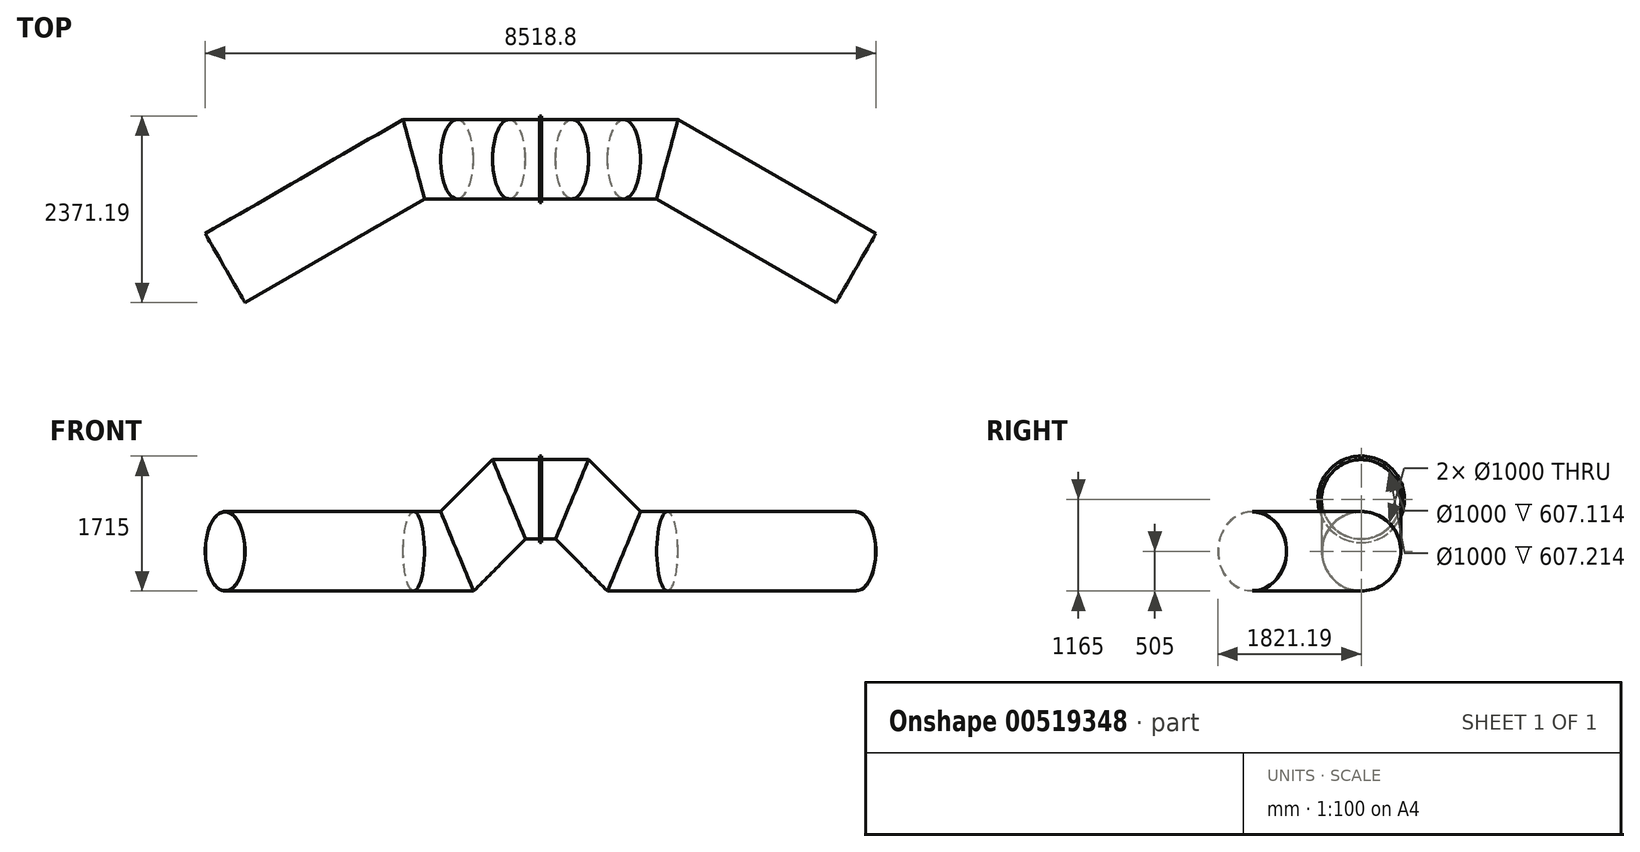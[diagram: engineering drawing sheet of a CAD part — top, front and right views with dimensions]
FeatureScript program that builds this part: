
annotation { "Feature Type Name" : "Feature", "Feature Type Description" : "" }
export const myFeature = defineFeature(function(context is Context, id is Id, definition is map)
    precondition{}
    {
        {
            var Q0;
            Q0=qCreatedBy(makeId("Top.planeOp"),FACE);
            var sketch = newSketch(context, id + "F0", { "sketchPlane" : qUnion([Q0])});
            skLineSegment(sketch, "E0", {"start": v(0, 0) * mm, "end": v(3000, 0) * mm, "construction": true});
            skSolve(sketch);
        }
        {
            var Q0;
            Q0=qCreatedBy(makeId("Top.planeOp"),FACE);
            cPlane(context, id + "F1", {"entities" : qUnion([Q0]), "cplaneType" : CPlaneType.OFFSET, "offset" : 660 * mm, "oppositeDirection" : true, "width" : 150 * mm, "height" : 150 * mm});
        }
        {
            var Q0;
            Q0=qCreatedBy(id+"F1.planeOp",FACE);
            var sketch = newSketch(context, id + "F2", { "sketchPlane" : qUnion([Q0])});
            skLineSegment(sketch, "E1", {"start": v(1610, 0) * mm, "end": v(4006.9, -1383.85) * mm});
            skLineSegment(sketch, "E2", {"start": v(4006.9, -1383.85) * mm, "end": v(3906.9, -1557.05) * mm, "construction": true});
            skSolve(sketch);
        }
        {
            var Q0;
            Q0=qCreatedBy(makeId("Front.planeOp"),FACE);
            var sketch = newSketch(context, id + "F3", { "sketchPlane" : qUnion([Q0])});
            skLineSegment(sketch, "E3", {"start": v(0, 0) * mm, "end": v(400, 0) * mm});
            skLineSegment(sketch, "E4", {"start": v(400, 0) * mm, "end": v(1060, -660) * mm});
            skLineSegment(sketch, "E5", {"start": v(1060, -660) * mm, "end": v(1610, -660) * mm});
            skPoint(sketch, "E6.0", {"position": v(1610, -660) * mm});
            skSolve(sketch);
        }
        {
            var Q0;
            Q0=qCreatedBy(makeId("Right.planeOp"),FACE);
            var sketch = newSketch(context, id + "F4", { "sketchPlane" : qUnion([Q0])});
            skCircle(sketch, "E7", {"center": v(0, 0) * mm, "radius": 500 * mm});
            skCircle(sketch, "E8", {"center": v(0, 0) * mm, "radius": 505 * mm});
            skSolve(sketch);
        }
        {
            var Q0;
            Q0 = qSketchRegion(id + "F4", true);
            var Q1;
            Q1 = qConstructionFilter(qBodyType(qCreatedBy(id + "F3" ,EDGE), BodyType.WIRE), ConstructionObject.NO);
            var Q2;
            Q2 = qConstructionFilter(qBodyType(qCreatedBy(id + "F2" ,EDGE), BodyType.WIRE), ConstructionObject.NO);
            sweep(context, id + "F5", {"profiles" : qUnion([Q0]), "path" : qUnion([Q1, Q2])});
        }
        {
            var Q0;
            Q0=makeQuery(id+"F5.opSweep","CAP_FACE",FACE,{"disambiguationData":[OSD([sQuery(id+"F3.wireOp",VERTEX,"E3.start"),sQuery(id+"F4.wireOp",EDGE,"E7"),sQuery(id+"F4.wireOp",EDGE,"E8")])],"isStart":true});
            var sketch = newSketch(context, id + "F6", { "sketchPlane" : qUnion([Q0])});
            skCircle(sketch, "E9.0", {"center": v(0, 0) * mm, "radius": 500 * mm});
            skCircle(sketch, "E10", {"center": v(0, 0) * mm, "radius": 550 * mm});
            skSolve(sketch);
        }
        {
            var Q0;
            Q0 = qSketchRegion(id + "F6", true);
            extrude(context, id + "F7", {"entities" : qUnion([Q0]), "operationType" : NewBodyOperationType.ADD, "oppositeDirection" : true, "depth" : 10 * mm, "offsetDistance" : 25 * mm});
        }
        {
            var Q0;
            Q0=makeQuery(id+"F5.opSweep","SWEPT_BODY",BODY,{"disambiguationData":[OSD([sQuery(id+"F2.wireOp",EDGE,"E1"),sQuery(id+"F4.wireOp",EDGE,"E7"),sQuery(id+"F4.wireOp",EDGE,"E8")])]});
            var Q1;
            Q1=qCreatedBy(makeId("Right.planeOp"),FACE);
            mirror(context, id + "F8", {"entities" : qUnion([Q0]), "mirrorPlane" : qUnion([Q1])});
        }
    });
